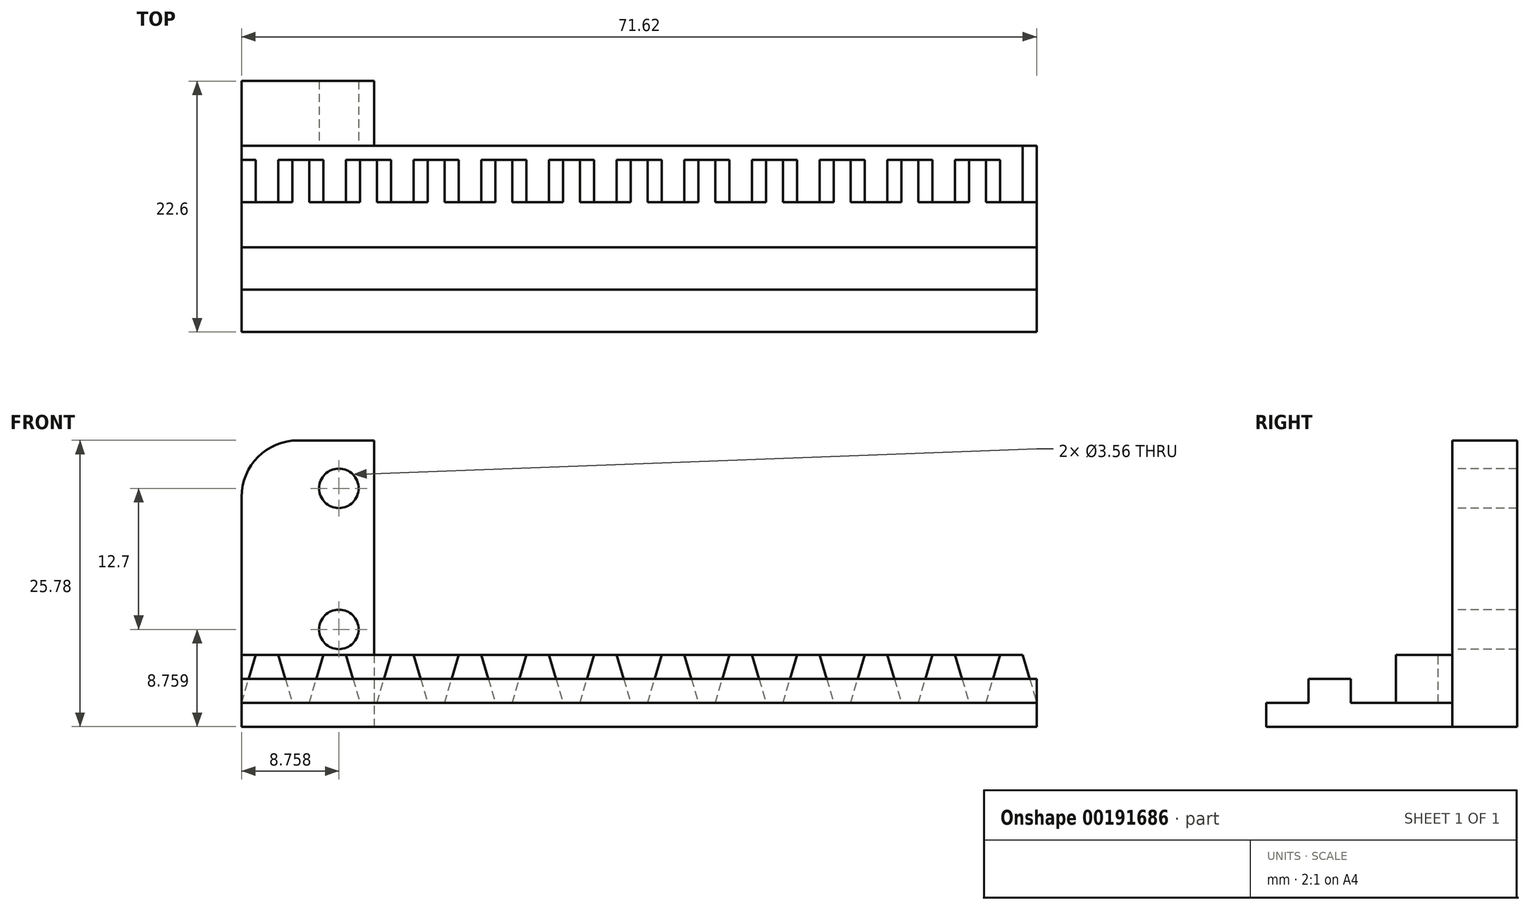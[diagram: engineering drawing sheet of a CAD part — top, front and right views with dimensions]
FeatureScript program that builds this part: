
annotation { "Feature Type Name" : "Feature", "Feature Type Description" : "" }
export const myFeature = defineFeature(function(context is Context, id is Id, definition is map)
    precondition{}
    {
        {
            var Q0;
            Q0=qCreatedBy(makeId("Front.planeOp"),FACE);
            var sketch = newSketch(context, id + "F0", { "sketchPlane" : qUnion([Q0])});
            skLineSegment(sketch, "E0.bottom", {"start": v(-38.44, 14.74) * mm, "end": v(33.18, 14.74) * mm});
            skLineSegment(sketch, "E0.top", {"start": v(-38.44, 16.9) * mm, "end": v(33.18, 16.9) * mm});
            skLineSegment(sketch, "E0.left", {"start": v(-38.44, 14.74) * mm, "end": v(-38.44, 16.9) * mm});
            skLineSegment(sketch, "E1", {"start": v(-38.44, 16.9) * mm, "end": v(-37.17, 21.21) * mm});
            skLineSegment(sketch, "E2", {"start": v(-37.17, 21.21) * mm, "end": v(-35.14, 21.21) * mm});
            skLineSegment(sketch, "E3", {"start": v(-35.14, 21.21) * mm, "end": v(-33.87, 16.9) * mm});
            skLineSegment(sketch, "E4", {"start": v(-38.44, 16.9) * mm, "end": v(-33.87, 16.9) * mm});
            skLineSegment(sketch, "E5", {"start": v(-36.16, 21.21) * mm, "end": v(-36.16, 16.9) * mm, "construction": true});
            skLineSegment(sketch, "E6", {"start": v(33.18, 14.74) * mm, "end": v(33.18, 16.9) * mm});
            skLineSegment(sketch, "E7.1.0.0", {"start": v(-29.05, 21.21) * mm, "end": v(-27.78, 16.9) * mm});
            skLineSegment(sketch, "E7.1.0.1", {"start": v(-32.35, 16.9) * mm, "end": v(-31.08, 21.21) * mm});
            skLineSegment(sketch, "E7.1.0.2", {"start": v(-31.08, 21.21) * mm, "end": v(-29.05, 21.21) * mm});
            skLineSegment(sketch, "E7.2.0.0", {"start": v(-22.95, 21.21) * mm, "end": v(-21.68, 16.9) * mm});
            skLineSegment(sketch, "E7.2.0.1", {"start": v(-26.25, 16.9) * mm, "end": v(-24.98, 21.21) * mm});
            skLineSegment(sketch, "E7.2.0.2", {"start": v(-24.98, 21.21) * mm, "end": v(-22.95, 21.21) * mm});
            skLineSegment(sketch, "E7.3.0.0", {"start": v(-16.85, 21.21) * mm, "end": v(-15.58, 16.9) * mm});
            skLineSegment(sketch, "E7.3.0.1", {"start": v(-20.16, 16.9) * mm, "end": v(-18.89, 21.21) * mm});
            skLineSegment(sketch, "E7.3.0.2", {"start": v(-18.89, 21.21) * mm, "end": v(-16.85, 21.21) * mm});
            skLineSegment(sketch, "E7.4.0.0", {"start": v(-10.76, 21.21) * mm, "end": v(-9.49, 16.9) * mm});
            skLineSegment(sketch, "E7.4.0.1", {"start": v(-14.06, 16.9) * mm, "end": v(-12.8, 21.21) * mm});
            skLineSegment(sketch, "E7.4.0.2", {"start": v(-12.8, 21.21) * mm, "end": v(-10.76, 21.21) * mm});
            skLineSegment(sketch, "E7.5.0.0", {"start": v(-4.66, 21.21) * mm, "end": v(-3.4, 16.9) * mm});
            skLineSegment(sketch, "E7.5.0.1", {"start": v(-7.96, 16.9) * mm, "end": v(-6.7, 21.21) * mm});
            skLineSegment(sketch, "E7.5.0.2", {"start": v(-6.7, 21.21) * mm, "end": v(-4.66, 21.21) * mm});
            skLineSegment(sketch, "E7.6.0.0", {"start": v(1.43, 21.21) * mm, "end": v(2.7, 16.9) * mm});
            skLineSegment(sketch, "E7.6.0.1", {"start": v(-1.87, 16.9) * mm, "end": v(-0.6, 21.21) * mm});
            skLineSegment(sketch, "E7.6.0.2", {"start": v(-0.6, 21.21) * mm, "end": v(1.43, 21.21) * mm});
            skLineSegment(sketch, "E7.7.0.0", {"start": v(7.53, 21.21) * mm, "end": v(8.8, 16.9) * mm});
            skLineSegment(sketch, "E7.7.0.1", {"start": v(4.23, 16.9) * mm, "end": v(5.5, 21.21) * mm});
            skLineSegment(sketch, "E7.7.0.2", {"start": v(5.5, 21.21) * mm, "end": v(7.53, 21.21) * mm});
            skLineSegment(sketch, "E7.8.0.0", {"start": v(13.63, 21.21) * mm, "end": v(14.9, 16.9) * mm});
            skLineSegment(sketch, "E7.8.0.1", {"start": v(10.32, 16.9) * mm, "end": v(11.6, 21.21) * mm});
            skLineSegment(sketch, "E7.8.0.2", {"start": v(11.6, 21.21) * mm, "end": v(13.63, 21.21) * mm});
            skLineSegment(sketch, "E7.9.0.0", {"start": v(19.72, 21.21) * mm, "end": v(21, 16.9) * mm});
            skLineSegment(sketch, "E7.9.0.1", {"start": v(16.42, 16.9) * mm, "end": v(17.69, 21.21) * mm});
            skLineSegment(sketch, "E7.9.0.2", {"start": v(17.69, 21.21) * mm, "end": v(19.72, 21.21) * mm});
            skLineSegment(sketch, "E7.10.0.0", {"start": v(25.82, 21.21) * mm, "end": v(27.09, 16.9) * mm});
            skLineSegment(sketch, "E7.10.0.1", {"start": v(22.52, 16.9) * mm, "end": v(23.79, 21.21) * mm});
            skLineSegment(sketch, "E7.10.0.2", {"start": v(23.79, 21.21) * mm, "end": v(25.82, 21.21) * mm});
            skLineSegment(sketch, "E7.11.0.0", {"start": v(31.91, 21.21) * mm, "end": v(33.18, 16.9) * mm});
            skLineSegment(sketch, "E7.11.0.1", {"start": v(28.61, 16.9) * mm, "end": v(29.88, 21.21) * mm});
            skLineSegment(sketch, "E7.11.0.2", {"start": v(29.88, 21.21) * mm, "end": v(31.91, 21.21) * mm});
            skLineSegment(sketch, "E7.direction1", {"start": v(-38.44, 16.9) * mm, "end": v(-32.35, 16.9) * mm, "construction": true});
            skPoint(sketch, "E8.centerSnap0", {"position": v(-38.44, 15.82) * mm});
            skSolve(sketch);
        }
        {
            var Q0;
            Q0=qSketchRegion(id+"F0",true);
            extrude(context, id + "F1", {"entities" : qUnion([Q0]), "depth" : 3.8 * mm});
        }
        {
            var Q0;
            Q0=qCreatedBy(makeId("Right.planeOp"),FACE);
            var Q1;
            Q1=makeQuery(id+"F1.opExtrude","CAP_VERTEX",VERTEX,{"disambiguationData":[OSD([sQuery(id+"F0.wireOp",EDGE,"E0.bottom"),sQuery(id+"F0.wireOp",EDGE,"E6")])],"isStart":false});
            cPlane(context, id + "F2", {"entities" : qUnion([Q0, Q1]), "cplaneType" : CPlaneType.PLANE_POINT, "offset" : 25.4 * mm, "width" : 152.4 * mm, "height" : 152.4 * mm});
        }
        {
            var Q0;
            Q0=qCreatedBy(id+"F2.planeOp",FACE);
            var sketch = newSketch(context, id + "F3", { "sketchPlane" : qUnion([Q0])});
            skLineSegment(sketch, "E9.0", {"start": v(-3.81, 14.74) * mm, "end": v(-3.81, 16.9) * mm});
            skLineSegment(sketch, "E10", {"start": v(-15.5, 16.9) * mm, "end": v(-11.68, 16.9) * mm});
            skLineSegment(sketch, "E11", {"start": v(-7.87, 16.9) * mm, "end": v(-7.87, 19.05) * mm});
            skLineSegment(sketch, "E12", {"start": v(-7.87, 19.05) * mm, "end": v(-11.68, 19.05) * mm});
            skLineSegment(sketch, "E13", {"start": v(-11.68, 19.05) * mm, "end": v(-11.68, 16.9) * mm});
            skLineSegment(sketch, "E14.trimOffspring", {"start": v(-7.87, 16.9) * mm, "end": v(-3.81, 16.9) * mm});
            skLineSegment(sketch, "E15", {"start": v(-3.81, 14.74) * mm, "end": v(-15.5, 14.74) * mm});
            skLineSegment(sketch, "E16", {"start": v(-15.5, 14.74) * mm, "end": v(-15.5, 16.9) * mm});
            skSolve(sketch);
        }
        {
            var Q0;
            Q0=qSketchRegion(id+"F3",true);
            var Q1;
            Q1=makeQuery(id+"F1.opExtrude","SWEPT_FACE",FACE,{"disambiguationData":[OSD([sQuery(id+"F0.wireOp",EDGE,"E0.left")])]});
            extrude(context, id + "F4", {"entities" : qUnion([Q0]), "operationType" : NewBodyOperationType.ADD, "endBound" : BoundingType.UP_TO_SURFACE, "oppositeDirection" : true, "endBoundEntityFace" : qUnion([Q1]), "depth" : 33.02 * mm});
        }
        {
            var Q0;
            Q0=makeQuery(id+"F1.opExtrude","CAP_FACE",FACE,{"disambiguationData":[OSD([sQuery(id+"F0.wireOp",EDGE,"E0.bottom"),sQuery(id+"F0.wireOp",EDGE,"E0.top"),sQuery(id+"F0.wireOp",EDGE,"E0.left"),sQuery(id+"F0.wireOp",EDGE,"E1"),sQuery(id+"F0.wireOp",EDGE,"E2"),sQuery(id+"F0.wireOp",EDGE,"E3"),sQuery(id+"F0.wireOp",EDGE,"E6"),sQuery(id+"F0.wireOp",EDGE,"E7.1.0.0"),sQuery(id+"F0.wireOp",EDGE,"E7.1.0.1"),sQuery(id+"F0.wireOp",EDGE,"E7.1.0.2"),sQuery(id+"F0.wireOp",EDGE,"E7.2.0.0"),sQuery(id+"F0.wireOp",EDGE,"E7.2.0.1"),sQuery(id+"F0.wireOp",EDGE,"E7.2.0.2"),sQuery(id+"F0.wireOp",EDGE,"E7.3.0.0"),sQuery(id+"F0.wireOp",EDGE,"E7.3.0.1"),sQuery(id+"F0.wireOp",EDGE,"E7.3.0.2"),sQuery(id+"F0.wireOp",EDGE,"E7.4.0.0"),sQuery(id+"F0.wireOp",EDGE,"E7.4.0.1"),sQuery(id+"F0.wireOp",EDGE,"E7.4.0.2"),sQuery(id+"F0.wireOp",EDGE,"E7.5.0.0"),sQuery(id+"F0.wireOp",EDGE,"E7.5.0.1"),sQuery(id+"F0.wireOp",EDGE,"E7.5.0.2"),sQuery(id+"F0.wireOp",EDGE,"E7.6.0.0"),sQuery(id+"F0.wireOp",EDGE,"E7.6.0.1"),sQuery(id+"F0.wireOp",EDGE,"E7.6.0.2"),sQuery(id+"F0.wireOp",EDGE,"E7.7.0.0"),sQuery(id+"F0.wireOp",EDGE,"E7.7.0.1"),sQuery(id+"F0.wireOp",EDGE,"E7.7.0.2"),sQuery(id+"F0.wireOp",EDGE,"E7.8.0.0"),sQuery(id+"F0.wireOp",EDGE,"E7.8.0.1"),sQuery(id+"F0.wireOp",EDGE,"E7.8.0.2"),sQuery(id+"F0.wireOp",EDGE,"E7.9.0.0"),sQuery(id+"F0.wireOp",EDGE,"E7.9.0.1"),sQuery(id+"F0.wireOp",EDGE,"E7.9.0.2"),sQuery(id+"F0.wireOp",EDGE,"E7.10.0.0"),sQuery(id+"F0.wireOp",EDGE,"E7.10.0.1"),sQuery(id+"F0.wireOp",EDGE,"E7.10.0.2"),sQuery(id+"F0.wireOp",EDGE,"E7.11.0.0"),sQuery(id+"F0.wireOp",EDGE,"E7.11.0.1"),sQuery(id+"F0.wireOp",EDGE,"E7.11.0.2")])],"isStart":true});
            var sketch = newSketch(context, id + "F5", { "sketchPlane" : qUnion([Q0])});
            skPoint(sketch, "E17.oppositeSnap0", {"position": v(23.97, 21.21) * mm});
            skLineSegment(sketch, "E17.bottom", {"start": v(38.44, 14.74) * mm, "end": v(-33.18, 14.74) * mm});
            skLineSegment(sketch, "E17.top", {"start": v(38.44, 21.21) * mm, "end": v(-33.18, 21.21) * mm});
            skLineSegment(sketch, "E17.left", {"start": v(38.44, 14.74) * mm, "end": v(38.44, 21.21) * mm});
            skLineSegment(sketch, "E17.right", {"start": v(-33.18, 14.74) * mm, "end": v(-33.18, 21.21) * mm});
            skLineSegment(sketch, "E18.0", {"start": v(-31.91, 21.21) * mm, "end": v(-33.18, 16.9) * mm});
            skLineSegment(sketch, "E19.0", {"start": v(38.44, 16.9) * mm, "end": v(37.17, 21.21) * mm});
            skSolve(sketch);
        }
        {
            var Q0;
            {var subQ1=sQuery(id+"F0.wireOp",EDGE,"E3");var subQ2=makeQuery(id+"F1.opExtrude","CAP_EDGE",EDGE,{"disambiguationData":[OSD([subQ1])],"isStart":true});Q0=makeQuery(id+"F5.imprint","IMPRINT",FACE,{"disambiguationData":[TD([[makeQuery(id+"F5.imprint","IMPRINT",EDGE,{"derivedFrom":subQ2}),-1.0]])]});}
            var Q1;
            {var subQ1=sQuery(id+"F0.wireOp",EDGE,"E7.1.0.0");var subQ2=makeQuery(id+"F1.opExtrude","CAP_EDGE",EDGE,{"disambiguationData":[OSD([subQ1])],"isStart":true});Q1=makeQuery(id+"F5.imprint","IMPRINT",FACE,{"disambiguationData":[TD([[makeQuery(id+"F5.imprint","IMPRINT",EDGE,{"derivedFrom":subQ2}),-1.0]])]});}
            var Q2;
            {var subQ1=sQuery(id+"F0.wireOp",EDGE,"E7.2.0.0");var subQ2=makeQuery(id+"F1.opExtrude","CAP_EDGE",EDGE,{"disambiguationData":[OSD([subQ1])],"isStart":true});Q2=makeQuery(id+"F5.imprint","IMPRINT",FACE,{"disambiguationData":[TD([[makeQuery(id+"F5.imprint","IMPRINT",EDGE,{"derivedFrom":subQ2}),-1.0]])]});}
            var Q3;
            {var subQ1=sQuery(id+"F0.wireOp",EDGE,"E7.3.0.0");var subQ2=makeQuery(id+"F1.opExtrude","CAP_EDGE",EDGE,{"disambiguationData":[OSD([subQ1])],"isStart":true});Q3=makeQuery(id+"F5.imprint","IMPRINT",FACE,{"disambiguationData":[TD([[makeQuery(id+"F5.imprint","IMPRINT",EDGE,{"derivedFrom":subQ2}),-1.0]])]});}
            var Q4;
            {var subQ1=sQuery(id+"F0.wireOp",EDGE,"E7.4.0.0");var subQ2=makeQuery(id+"F1.opExtrude","CAP_EDGE",EDGE,{"disambiguationData":[OSD([subQ1])],"isStart":true});Q4=makeQuery(id+"F5.imprint","IMPRINT",FACE,{"disambiguationData":[TD([[makeQuery(id+"F5.imprint","IMPRINT",EDGE,{"derivedFrom":subQ2}),-1.0]])]});}
            var Q5;
            {var subQ1=sQuery(id+"F0.wireOp",EDGE,"E7.5.0.0");var subQ2=makeQuery(id+"F1.opExtrude","CAP_EDGE",EDGE,{"disambiguationData":[OSD([subQ1])],"isStart":true});Q5=makeQuery(id+"F5.imprint","IMPRINT",FACE,{"disambiguationData":[TD([[makeQuery(id+"F5.imprint","IMPRINT",EDGE,{"derivedFrom":subQ2}),-1.0]])]});}
            var Q6;
            {var subQ1=sQuery(id+"F0.wireOp",EDGE,"E7.6.0.0");var subQ2=makeQuery(id+"F1.opExtrude","CAP_EDGE",EDGE,{"disambiguationData":[OSD([subQ1])],"isStart":true});Q6=makeQuery(id+"F5.imprint","IMPRINT",FACE,{"disambiguationData":[TD([[makeQuery(id+"F5.imprint","IMPRINT",EDGE,{"derivedFrom":subQ2}),-1.0]])]});}
            var Q7;
            {var subQ1=sQuery(id+"F0.wireOp",EDGE,"E7.7.0.0");var subQ2=makeQuery(id+"F1.opExtrude","CAP_EDGE",EDGE,{"disambiguationData":[OSD([subQ1])],"isStart":true});Q7=makeQuery(id+"F5.imprint","IMPRINT",FACE,{"disambiguationData":[TD([[makeQuery(id+"F5.imprint","IMPRINT",EDGE,{"derivedFrom":subQ2}),-1.0]])]});}
            var Q8;
            {var subQ1=sQuery(id+"F0.wireOp",EDGE,"E7.8.0.0");var subQ2=makeQuery(id+"F1.opExtrude","CAP_EDGE",EDGE,{"disambiguationData":[OSD([subQ1])],"isStart":true});Q8=makeQuery(id+"F5.imprint","IMPRINT",FACE,{"disambiguationData":[TD([[makeQuery(id+"F5.imprint","IMPRINT",EDGE,{"derivedFrom":subQ2}),-1.0]])]});}
            var Q9;
            {var subQ1=sQuery(id+"F0.wireOp",EDGE,"E7.9.0.0");var subQ2=makeQuery(id+"F1.opExtrude","CAP_EDGE",EDGE,{"disambiguationData":[OSD([subQ1])],"isStart":true});Q9=makeQuery(id+"F5.imprint","IMPRINT",FACE,{"disambiguationData":[TD([[makeQuery(id+"F5.imprint","IMPRINT",EDGE,{"derivedFrom":subQ2}),-1.0]])]});}
            var Q10;
            {var subQ1=sQuery(id+"F0.wireOp",EDGE,"E7.10.0.0");var subQ2=makeQuery(id+"F1.opExtrude","CAP_EDGE",EDGE,{"disambiguationData":[OSD([subQ1])],"isStart":true});Q10=makeQuery(id+"F5.imprint","IMPRINT",FACE,{"disambiguationData":[TD([[makeQuery(id+"F5.imprint","IMPRINT",EDGE,{"derivedFrom":subQ2}),-1.0]])]});}
            var Q11;
            {var subQ42=sQuery(id+"F5.wireOp",EDGE,"E17.bottom");Q11=makeQuery(id+"F5.imprint","IMPRINT",FACE,{"disambiguationData":[TD([[makeQuery(id+"F5.imprint","IMPRINT",EDGE,{"derivedFrom":subQ42}),-1.0]])]});}
            var Q12;
            {var subQ0=sQuery(id+"F5.wireOp",EDGE,"E19.0");Q12=makeQuery(id+"F5.imprint","IMPRINT",FACE,{"disambiguationData":[TD([[makeQuery(id+"F5.imprint","IMPRINT",EDGE,{"derivedFrom":subQ0}),-1.0]])]});}
            extrude(context, id + "F6", {"entities" : qUnion([Q0, Q1, Q2, Q3, Q4, Q5, Q6, Q7, Q8, Q9, Q10, Q11, Q12]), "operationType" : NewBodyOperationType.ADD, "depth" : 1.27 * mm});
        }
        {
            var Q0;
            Q0=makeQuery(id+"F6.opExtrude","CAP_FACE",FACE,{"disambiguationData":[OSD([sQuery(id+"F5.wireOp",EDGE,"E17.bottom"),sQuery(id+"F5.wireOp",EDGE,"E17.top"),sQuery(id+"F5.wireOp",EDGE,"E17.left"),sQuery(id+"F5.wireOp",EDGE,"E17.right")])],"isStart":false});
            var sketch = newSketch(context, id + "F7", { "sketchPlane" : qUnion([Q0])});
            skLineSegment(sketch, "E20", {"start": v(38.44, 21.21) * mm, "end": v(38.44, 40.52) * mm});
            skCircle(sketch, "E21", {"center": v(29.68, 36.2) * mm, "radius": 1.78 * mm});
            skCircle(sketch, "E22", {"center": v(29.68, 23.5) * mm, "radius": 1.78 * mm});
            skLineSegment(sketch, "E23.2", {"start": v(38.44, 14.74) * mm, "end": v(38.44, 21.21) * mm});
            skLineSegment(sketch, "E24", {"start": v(38.44, 40.52) * mm, "end": v(26.5, 40.52) * mm});
            skLineSegment(sketch, "E25", {"start": v(26.5, 40.52) * mm, "end": v(26.5, 14.74) * mm});
            skLineSegment(sketch, "E26", {"start": v(26.5, 14.74) * mm, "end": v(38.44, 14.74) * mm});
            skSolve(sketch);
        }
        {
            var Q0;
            Q0 = qSketchRegion(id + "F7", true);
            extrude(context, id + "F8", {"entities" : qUnion([Q0]), "operationType" : NewBodyOperationType.ADD, "depth" : 5.84 * mm});
        }
        {
            var Q0;
            Q0=makeQuery(id+"F8.opExtrude","SWEPT_EDGE",EDGE,{"disambiguationData":[OSD([sQuery(id+"F7.wireOp",EDGE,"E20"),sQuery(id+"F7.wireOp",EDGE,"E24")])]});
            fillet(context, id + "F9", {"entities" : qUnion([Q0]), "radius" : 5.08 * mm, "tangentPropagation" : true, "allowEdgeOverflow" : false});
        }
    });
